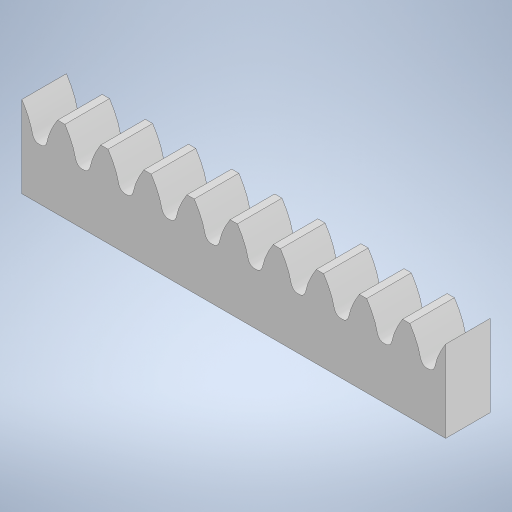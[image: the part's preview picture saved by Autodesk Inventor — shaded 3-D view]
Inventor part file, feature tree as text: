
AUTODESK INVENTOR PART (.ipt)
format: ipt  version: 2023 (Build 270158000, 158)  size: 291,840 bytes
history: native  units: mm
features: extrude x3, sketch x1, pattern_linear x1
ambient origin geometry x8: Origin, YZ Plane, XZ Plane, XY Plane, X Axis, Y Axis, Z Axis, Center Point
bodies: Body1 (feature_tree)
feature tree (5):
  sketch  "Sketch1"  dims[d7=61.768mm d9=2.0mm d10=2.0mm d11=1.0mm d12=5.5mm d13=1.0mm d14=6.5mm d15=0.0mm d16=2.0mm d17=0.0mm d18=0.0mm d19=0.0mm d20=100.0mm d22=6.283mm]
  extrude  "Extrusion3"  Depth=2.0mm
  extrude  "Extrusion4"  Depth=2.0mm
  extrude  "Extrusion5"  Depth=1.0mm
  pattern_linear  "Rectangular Pattern2"  Spacing1=5.5mm  [1 undecoded]
note: 1 required parameter value undecoded (feature->parameter linkage not recoverable at this tier; creation-order binding heuristic only, values carry confidence <= 0.55)
